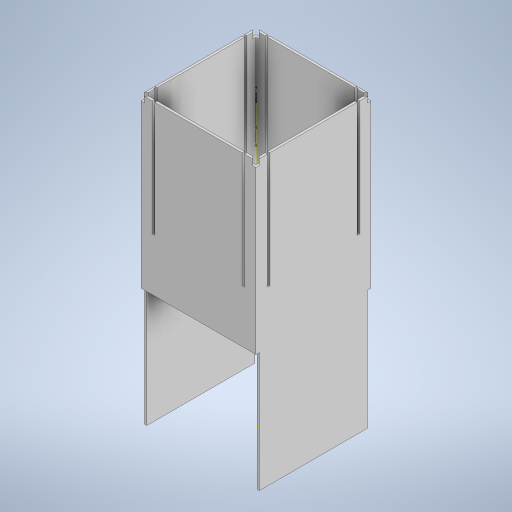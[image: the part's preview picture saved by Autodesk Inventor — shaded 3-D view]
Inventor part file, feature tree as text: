
AUTODESK INVENTOR PART (.ipt)
format: ipt  version: 2024.3 (Build 283343000, 343)  size: 314,368 bytes
history: native  units: mm
features: extrude x6, sketch x6, mirror x3, plane x2
ambient origin geometry x8: Origin, YZ Plane, XZ Plane, XY Plane, X Axis, Y Axis, Z Axis, Center Point
bodies: Solid1 (feature_tree)
feature tree (17):
  extrude  "Extrusion1"  Depth=100.0mm
  extrude  "Extrusion2"  Depth=250.0mm TaperAngle=0.0deg
  mirror  "Mirror1"
  extrude  "Extrusion3"  Depth=104.0mm
  mirror  "Mirror2"
  extrude  "Extrusion4"  Depth=100.0mm
  mirror  "Mirror3"
  plane  "Work Plane1"
  sketch  "Sketch5"  dims[d10=2.0mm d11=10.0mm]
  extrude  "Extrusion5"  Depth=10.0mm
  plane  "Work Plane2"
  extrude  "Extrusion6"  Depth=10.0mm
  sketch  "Sketch1"  dims[d0=100.0mm d1=100.0mm]
  sketch  "Sketch2"  dims[d2=2.0mm d3=250.0mm d4=0.0mm]
  sketch  "Sketch3"  dims[d5=3.0mm d6=104.0mm]
  sketch  "Sketch4"  dims[d7=220.0mm d8=0.0mm d9=100.0mm]
  sketch  "Sketch6"  dims[d12=220.0mm d13=0.0mm d14=10.0mm d15=2.0mm d16=100.0mm d17=0.0mm d18=220.0mm d19=0.0mm d20=5.0mm d21=4.0mm d22=0.0mm d23=0.0mm d24=220.0mm d25=0.0mm d26=4.0mm d27=5.0mm d28=0.0mm d29=220.0mm d30=0.0mm]
